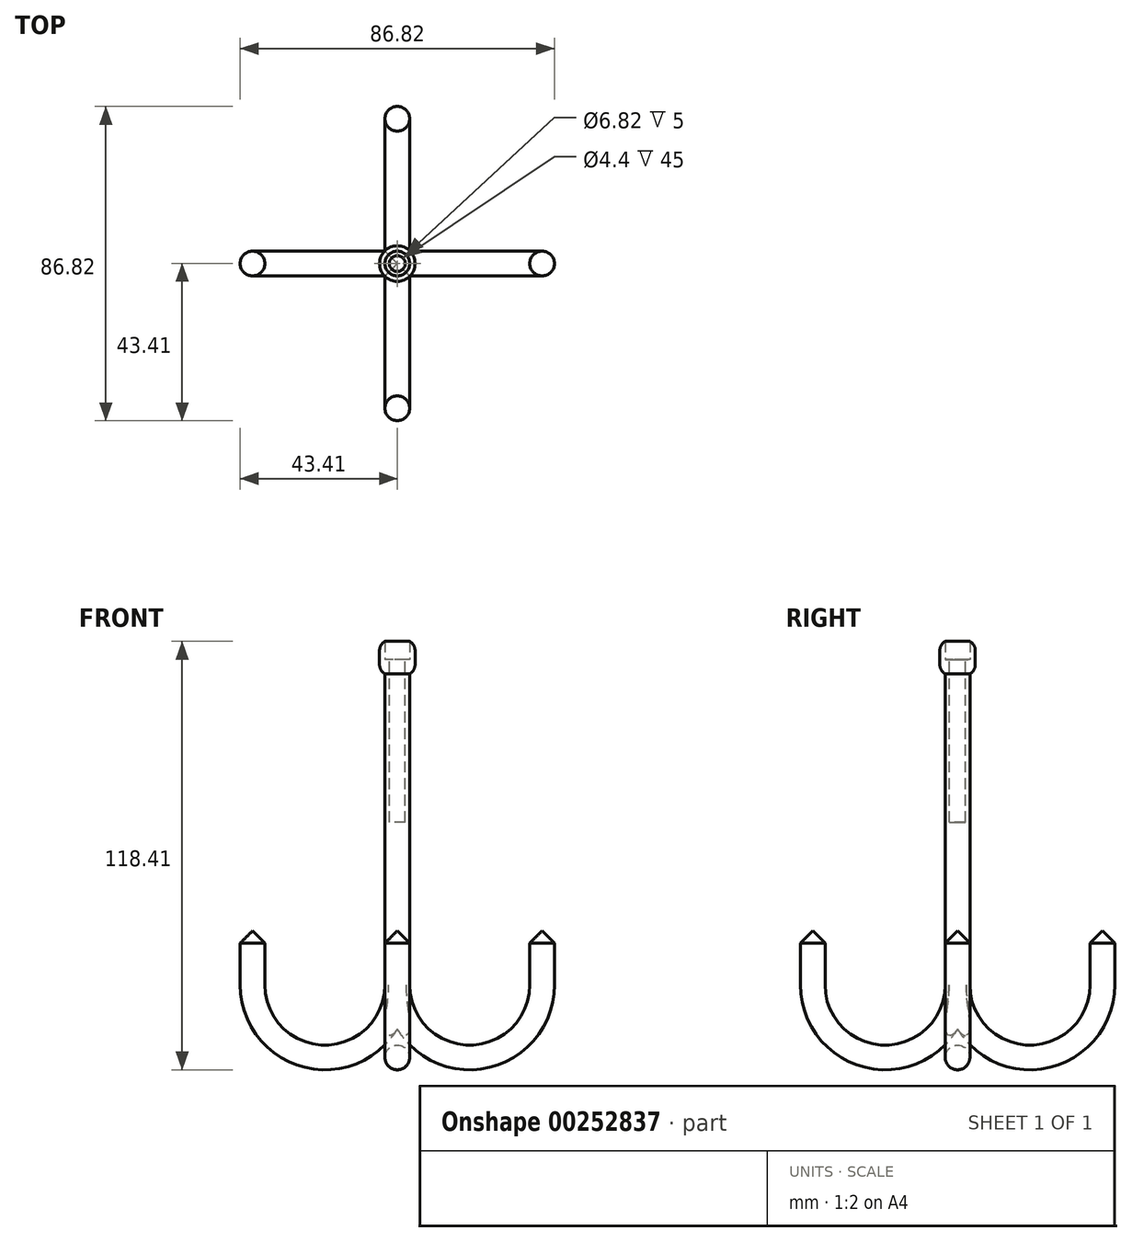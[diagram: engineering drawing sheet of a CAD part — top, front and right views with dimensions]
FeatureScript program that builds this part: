
annotation { "Feature Type Name" : "Feature", "Feature Type Description" : "" }
export const myFeature = defineFeature(function(context is Context, id is Id, definition is map)
    precondition{}
    {
        {
            var Q0;
            Q0=qCreatedBy(makeId("Top.planeOp"),FACE);
            var sketch = newSketch(context, id + "F0", { "sketchPlane" : qUnion([Q0])});
            skCircle(sketch, "E0", {"center": v(0, 0) * mm, "radius": 3.4 * mm});
            skSolve(sketch);
        }
        {
            var Q0;
            Q0=qCreatedBy(makeId("Front.planeOp"),FACE);
            var sketch = newSketch(context, id + "F1", { "sketchPlane" : qUnion([Q0])});
            skLineSegment(sketch, "E1", {"start": v(0, 0) * mm, "end": v(0, -90) * mm});
            skArc(sketch, "E2", {"start": v(0, -90) * mm, "mid": v(20, -110) * mm, "end": v(40, -90) * mm});
            skLineSegment(sketch, "E3", {"start": v(40, -90) * mm, "end": v(40, -75) * mm});
            skSolve(sketch);
        }
        {
            var Q0;
            Q0=makeQuery(id+"F0.imprint","IMPRINT",FACE,{"disambiguationData":[TD([[makeQuery(id+"F0.imprint","IMPRINT",EDGE,{"derivedFrom":sQuery(id+"F0.wireOp",EDGE,"E0")}),1.0]])]});
            var Q1;
            Q1=sQuery(id+"F1.wireOp",EDGE,"E1");
            var Q2;
            Q2=sQuery(id+"F1.wireOp",EDGE,"E2");
            var Q3;
            Q3=sQuery(id+"F1.wireOp",EDGE,"E3");
            sweep(context, id + "F2", {"profiles" : qUnion([Q0]), "path" : qUnion([Q1, Q2, Q3])});
        }
        {
            var Q0;
            Q0=makeQuery(id+"F2.opSweep","SWEPT_BODY",BODY,{"disambiguationData":[OSD([sQuery(id+"F0.wireOp",EDGE,"E0"),sQuery(id+"F1.wireOp",EDGE,"E3")])]});
            var Q1;
            Q1=sQuery(id+"F1.wireOp",EDGE,"E1");
            circularPattern(context, id + "F3", {"operationType" : NewBodyOperationType.ADD, "entities" : qUnion([Q0]), "axis" : qUnion([Q1]), "angle" : 360 * degree, "instanceCount" : 4, "equalSpace" : true});
        }
        {
            var Q0;
            Q0=makeQuery(id+"F2.opSweep","SWEPT_FACE",FACE,{"disambiguationData":[OSD([sQuery(id+"F0.wireOp",EDGE,"E0"),sQuery(id+"F1.wireOp",EDGE,"E3")])]});
            var Q1;
            Q1=makeQuery(id+"F3.opPattern","COPY",FACE,{"derivedFrom":makeQuery(id+"F2.opSweep","SWEPT_FACE",FACE,{"disambiguationData":[OSD([sQuery(id+"F0.wireOp",EDGE,"E0"),sQuery(id+"F1.wireOp",EDGE,"E3")])]}),"instanceName":"2"});
            var Q2;
            Q2=makeQuery(id+"F3.opPattern","COPY",FACE,{"derivedFrom":makeQuery(id+"F2.opSweep","SWEPT_FACE",FACE,{"disambiguationData":[OSD([sQuery(id+"F0.wireOp",EDGE,"E0"),sQuery(id+"F1.wireOp",EDGE,"E3")])]}),"instanceName":"3"});
            var Q3;
            Q3=makeQuery(id+"F3.opPattern","COPY",FACE,{"derivedFrom":makeQuery(id+"F2.opSweep","SWEPT_FACE",FACE,{"disambiguationData":[OSD([sQuery(id+"F0.wireOp",EDGE,"E0"),sQuery(id+"F1.wireOp",EDGE,"E3")])]}),"instanceName":"1"});
            chamfer(context, id + "F4", {"entities" : qUnion([Q0, Q1, Q2, Q3]), "width" : (6.82 / 2) * mm, "tangentPropagation" : true});
        }
        {
            var Q0;
            Q0=makeQuery(id+"F2.opSweep","CAP_FACE",FACE,{"disambiguationData":[OSD([sQuery(id+"F0.wireOp",EDGE,"E0"),sQuery(id+"F1.wireOp",VERTEX,"E1.start")])],"isStart":true});
            var sketch = newSketch(context, id + "F5", { "sketchPlane" : qUnion([Q0])});
            skCircle(sketch, "E4", {"center": v(0, 0) * mm, "radius": 2.2 * mm});
            skSolve(sketch);
        }
        {
            var Q0;
            Q0=makeQuery(id+"F5.imprint","IMPRINT",FACE,{"disambiguationData":[TD([[makeQuery(id+"F5.imprint","IMPRINT",EDGE,{"derivedFrom":sQuery(id+"F5.wireOp",EDGE,"E4")}),1.0]])]});
            var Q1;
            Q1=sQuery(id+"F5.wireOp",EDGE,"E4");
            extrude(context, id + "F6", {"entities" : qUnion([Q0]), "operationType" : NewBodyOperationType.REMOVE, "surfaceEntities" : qUnion([Q1]), "oppositeDirection" : true, "depth" : 45 * mm});
        }
        {
            var Q0;
            Q0=makeQuery(id+"F2.opSweep","CAP_FACE",FACE,{"disambiguationData":[OSD([sQuery(id+"F0.wireOp",EDGE,"E0"),sQuery(id+"F1.wireOp",VERTEX,"E1.start")])],"isStart":true});
            var sketch = newSketch(context, id + "F7", { "sketchPlane" : qUnion([Q0])});
            skCircle(sketch, "E5", {"center": v(0, 0) * mm, "radius": 4.9 * mm});
            skCircle(sketch, "E6", {"center": v(0, 0) * mm, "radius": 2.2 * mm});
            skSolve(sketch);
        }
        {
            var Q0;
            Q0=makeQuery(id+"F7.imprint","IMPRINT",FACE,{"disambiguationData":[TD([[makeQuery(id+"F7.imprint","IMPRINT",EDGE,{"derivedFrom":sQuery(id+"F7.wireOp",EDGE,"E6")}),1.0]])]});
            extrude(context, id + "F8", {"entities" : qUnion([Q0]), "oppositeDirection" : true, "depth" : 45 * mm});
        }
        {
            var Q0;
            Q0=makeQuery(id+"F7.imprint","IMPRINT",FACE,{"disambiguationData":[TD([[makeQuery(id+"F7.imprint","IMPRINT",EDGE,{"derivedFrom":sQuery(id+"F7.wireOp",EDGE,"E5")}),1.0]])]});
            extrude(context, id + "F9", {"entities" : qUnion([Q0]), "operationType" : NewBodyOperationType.ADD, "oppositeDirection" : true, "depth" : 4 * mm});
        }
        {
            var Q0;
            Q0=makeQuery(id+"F7.imprint","IMPRINT",FACE,{"disambiguationData":[TD([[makeQuery(id+"F7.imprint","IMPRINT",EDGE,{"derivedFrom":sQuery(id+"F7.wireOp",EDGE,"E5")}),1.0]])]});
            extrude(context, id + "F10", {"entities" : qUnion([Q0]), "operationType" : NewBodyOperationType.ADD, "depth" : 5 * mm});
        }
        {
            var Q0;
            {var subQ0=sQuery(id+"F7.wireOp",EDGE,"E5");Q0=makeQuery(id+"F10.boolean.opBoolean","MERGE",FACE,{"derivedFrom":[makeQuery(id+"F9.opExtrude","SWEPT_FACE",FACE,{"disambiguationData":[OSD([subQ0])]}),makeQuery(id+"F10.opExtrude","SWEPT_FACE",FACE,{"disambiguationData":[OSD([subQ0])]})]});}
            fillet(context, id + "F11", {"entities" : qUnion([Q0]), "radius" : 3 * mm, "tangentPropagation" : true, "allowEdgeOverflow" : false});
        }
    });
